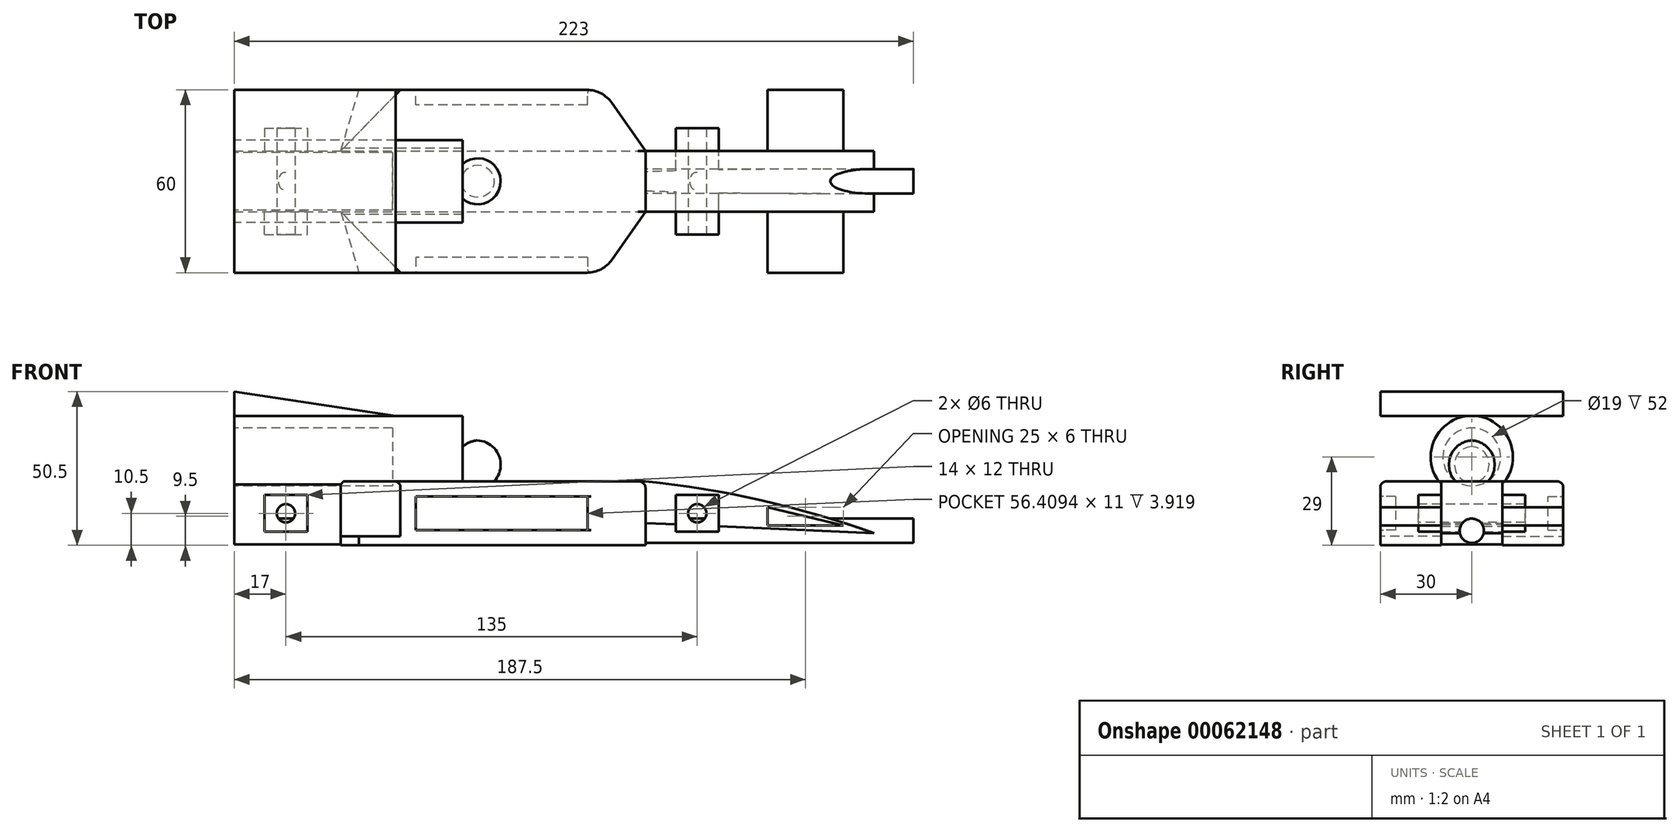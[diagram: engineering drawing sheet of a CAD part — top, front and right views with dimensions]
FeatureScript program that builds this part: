
annotation { "Feature Type Name" : "Feature", "Feature Type Description" : "" }
export const myFeature = defineFeature(function(context is Context, id is Id, definition is map)
    precondition{}
    {
        {
            var Q0;
            Q0=qCreatedBy(makeId("Front.planeOp"),FACE);
            var sketch = newSketch(context, id + "F0", { "sketchPlane" : qUnion([Q0])});
            skLineSegment(sketch, "E0.bottom", {"start": v(0, -8) * mm, "end": v(135, -8) * mm});
            skLineSegment(sketch, "E0.top", {"start": v(0, -28.73) * mm, "end": v(135, -28.73) * mm});
            skLineSegment(sketch, "E0.left", {"start": v(0, -8) * mm, "end": v(0, -28.73) * mm});
            skLineSegment(sketch, "E1", {"start": v(135, -28.73) * mm, "end": v(135, -21.73) * mm});
            skLineSegment(sketch, "E2", {"start": v(135, -21.73) * mm, "end": v(210, -25) * mm});
            skArc(sketch, "E3", {"start": v(210, -25) * mm, "mid": v(173.01, -14.23) * mm, "end": v(135, -8) * mm});
            skSolve(sketch);
        }
        {
            var Q0;
            Q0=makeQuery(id+"F0.imprint","IMPRINT",FACE,{"disambiguationData":[TD([[makeQuery(id+"F0.imprint","IMPRINT",EDGE,{"derivedFrom":sQuery(id+"F0.wireOp",EDGE,"E0.bottom")}),-1.0]])]});
            extrude(context, id + "F1", {"entities" : qUnion([Q0]), "depth" : 10 * mm});
        }
        {
            var Q0;
            Q0=makeQuery(id+"F1.opExtrude","SWEPT_FACE",FACE,{"disambiguationData":[OSD([sQuery(id+"F0.wireOp",EDGE,"E0.bottom")])]});
            var sketch = newSketch(context, id + "F2", { "sketchPlane" : qUnion([Q0])});
            skLineSegment(sketch, "E4", {"start": v(35, -10) * mm, "end": v(41, -30) * mm});
            skLineSegment(sketch, "E5", {"start": v(41, -30) * mm, "end": v(121, -30) * mm});
            skLineSegment(sketch, "E6", {"start": v(135, -10) * mm, "end": v(35, -10) * mm});
            skLineSegment(sketch, "E7", {"start": v(121, -30) * mm, "end": v(135, -10) * mm});
            skSolve(sketch);
        }
        {
            var Q0;
            Q0=makeQuery(id+"F2.imprint","IMPRINT",FACE,{"disambiguationData":[TD([[makeQuery(id+"F2.imprint","IMPRINT",EDGE,{"derivedFrom":sQuery(id+"F2.wireOp",EDGE,"E4")}),1.0]])]});
            extrude(context, id + "F3", {"entities" : qUnion([Q0]), "oppositeDirection" : true, "depth" : 21 * mm});
        }
        {
            var Q0;
            Q0=makeQuery(id+"F3.opExtrude","CAP_FACE",FACE,{"disambiguationData":[OSD([sQuery(id+"F2.wireOp",EDGE,"E4"),sQuery(id+"F2.wireOp",EDGE,"E5"),sQuery(id+"F2.wireOp",EDGE,"E6"),sQuery(id+"F2.wireOp",EDGE,"E7")])],"isStart":true});
            var sketch = newSketch(context, id + "F4", { "sketchPlane" : qUnion([Q0])});
            skLineSegment(sketch, "E8", {"start": v(0, -9.96) * mm, "end": v(35, -10) * mm});
            skLineSegment(sketch, "E9", {"start": v(35, -10) * mm, "end": v(72.36, -48.15) * mm});
            skLineSegment(sketch, "E10", {"start": v(72.36, -48.15) * mm, "end": v(0, -9.96) * mm});
            skSolve(sketch);
        }
        {
            var Q0;
            {var subQ1=makeQuery(id+"F3.opExtrude","CAP_EDGE",EDGE,{"disambiguationData":[OSD([sQuery(id+"F2.wireOp",EDGE,"E4")])],"isStart":true});Q0=makeQuery(id+"F4.imprint","IMPRINT",FACE,{"disambiguationData":[TD([[makeQuery(id+"F4.imprint","IMPRINT",EDGE,{"derivedFrom":subQ1}),1.0]])]});}
            extrude(context, id + "F5", {"entities" : qUnion([Q0]), "operationType" : NewBodyOperationType.REMOVE, "oppositeDirection" : true, "depth" : 18 * mm});
        }
        {
            var Q0;
            Q0=makeQuery(id+"F3.opExtrude","SWEPT_FACE",FACE,{"disambiguationData":[OSD([sQuery(id+"F2.wireOp",EDGE,"E5")])]});
            var sketch = newSketch(context, id + "F6", { "sketchPlane" : qUnion([Q0])});
            skLineSegment(sketch, "E11.0", {"start": v(59.59, -13) * mm, "end": v(59.59, -24) * mm});
            skLineSegment(sketch, "E11.2", {"start": v(59.59, -24) * mm, "end": v(116, -24) * mm});
            skLineSegment(sketch, "E11.4", {"start": v(116, -24) * mm, "end": v(116, -13) * mm});
            skLineSegment(sketch, "E11.5", {"start": v(116, -13) * mm, "end": v(59.59, -13) * mm});
            skSolve(sketch);
        }
        {
            var Q0;
            Q0=makeQuery(id+"F6.imprint","IMPRINT",FACE,{"disambiguationData":[TD([[makeQuery(id+"F6.imprint","IMPRINT",EDGE,{"derivedFrom":sQuery(id+"F6.wireOp",EDGE,"E11.0")}),1.0]])]});
            extrude(context, id + "F7", {"entities" : qUnion([Q0]), "operationType" : NewBodyOperationType.REMOVE, "oppositeDirection" : true, "depth" : 5 * mm});
        }
        {
            var Q0;
            Q0=qCreatedBy(makeId("Front.planeOp"),FACE);
            var sketch = newSketch(context, id + "F8", { "sketchPlane" : qUnion([Q0])});
            skLineSegment(sketch, "E12.bottom", {"start": v(0, 0) * mm, "end": v(75, 0) * mm});
            skLineSegment(sketch, "E12.top", {"start": v(0, 13.5) * mm, "end": v(75, 13.5) * mm});
            skLineSegment(sketch, "E12.left", {"start": v(0, 0) * mm, "end": v(0, 13.5) * mm});
            skLineSegment(sketch, "E12.right", {"start": v(75, 0) * mm, "end": v(75, 13.5) * mm});
            skSolve(sketch);
        }
        {
            var Q0;
            Q0=makeQuery(id+"F8.imprint","IMPRINT",FACE,{"disambiguationData":[TD([[makeQuery(id+"F8.imprint","IMPRINT",EDGE,{"derivedFrom":sQuery(id+"F8.wireOp",EDGE,"E12.bottom")}),1.0]])]});
            var Q1;
            Q1=sQuery(id+"F8.wireOp",EDGE,"E12.bottom");
            revolve(context, id + "F9", {"entities" : qUnion([Q0]), "axis" : qUnion([Q1]), "revolveType" : RevolveType.ONE_DIRECTION, "angle" : 180 * degree});
        }
        {
            var Q0;
            Q0=makeQuery(id+"F9.opRevolve","SWEPT_FACE",FACE,{"disambiguationData":[OSD([sQuery(id+"F8.wireOp",EDGE,"E12.left")])]});
            var sketch = newSketch(context, id + "F10", { "sketchPlane" : qUnion([Q0])});
            skArc(sketch, "E13", {"start": v(0, -9.5) * mm, "mid": v(9.5, 0) * mm, "end": v(0, 9.5) * mm});
            skLineSegment(sketch, "E14", {"start": v(0, 9.5) * mm, "end": v(0, -9.5) * mm});
            skSolve(sketch);
        }
        {
            var Q0;
            Q0=makeQuery(id+"F10.imprint","IMPRINT",FACE,{"disambiguationData":[TD([[makeQuery(id+"F10.imprint","IMPRINT",EDGE,{"derivedFrom":sQuery(id+"F10.wireOp",EDGE,"E13")}),1.0]])]});
            extrude(context, id + "F11", {"entities" : qUnion([Q0]), "operationType" : NewBodyOperationType.REMOVE, "oppositeDirection" : true, "depth" : 52 * mm});
        }
        {
            var Q0;
            Q0=qCreatedBy(makeId("Front.planeOp"),FACE);
            var sketch = newSketch(context, id + "F12", { "sketchPlane" : qUnion([Q0])});
            skLineSegment(sketch, "E15.bottom", {"start": v(145, -12.5) * mm, "end": v(159, -12.5) * mm});
            skLineSegment(sketch, "E15.top", {"start": v(145, -24.5) * mm, "end": v(159, -24.5) * mm});
            skLineSegment(sketch, "E15.left", {"start": v(145, -12.5) * mm, "end": v(145, -24.5) * mm});
            skLineSegment(sketch, "E15.right", {"start": v(159, -12.5) * mm, "end": v(159, -24.5) * mm});
            skLineSegment(sketch, "E16.1.0.0", {"start": v(24, -12.5) * mm, "end": v(24, -24.5) * mm});
            skLineSegment(sketch, "E16.1.0.1", {"start": v(10, -12.5) * mm, "end": v(24, -12.5) * mm});
            skLineSegment(sketch, "E16.1.0.2", {"start": v(10, -12.5) * mm, "end": v(10, -24.5) * mm});
            skLineSegment(sketch, "E16.1.0.3", {"start": v(10, -24.5) * mm, "end": v(24, -24.5) * mm});
            skLineSegment(sketch, "E16.direction1", {"start": v(159, -24.5) * mm, "end": v(24, -24.5) * mm, "construction": true});
            skSolve(sketch);
        }
        {
            var Q0;
            Q0 = qSketchRegion(id + "F12", true);
            extrude(context, id + "F13", {"entities" : qUnion([Q0]), "depth" : 17.5 * mm});
        }
        {
            var Q0;
            Q0=makeQuery(id+"F3.opExtrude","SWEPT_EDGE",EDGE,{"disambiguationData":[OSD([sQuery(id+"F2.wireOp",EDGE,"E5"),sQuery(id+"F2.wireOp",EDGE,"E7")])]});
            var Q1;
            Q1=makeQuery(id+"F5.boolean.opBoolean","COPY",EDGE,{"derivedFrom":makeQuery(id+"F5.opExtrude","SWEPT_EDGE",EDGE,{"disambiguationData":[OSD([sQuery(id+"F2.wireOp",EDGE,"E5"),sQuery(id+"F4.wireOp",EDGE,"E9")])]})});
            fillet(context, id + "F14", {"entities" : qUnion([Q0, Q1]), "radius" : 10 * mm, "tangentPropagation" : true, "allowEdgeOverflow" : false});
        }
        {
            var Q0;
            Q0=qCreatedBy(makeId("Front.planeOp"),FACE);
            var sketch = newSketch(context, id + "F15", { "sketchPlane" : qUnion([Q0])});
            skLineSegment(sketch, "E17", {"start": v(0, 13.5) * mm, "end": v(53, 13.5) * mm});
            skLineSegment(sketch, "E18", {"start": v(53, 13.5) * mm, "end": v(0, 21.5) * mm});
            skLineSegment(sketch, "E19", {"start": v(0, 21.5) * mm, "end": v(0, 13.5) * mm});
            skSolve(sketch);
        }
        {
            var Q0;
            Q0=makeQuery(id+"F15.imprint","IMPRINT",FACE,{"disambiguationData":[TD([[makeQuery(id+"F15.imprint","IMPRINT",EDGE,{"derivedFrom":sQuery(id+"F15.wireOp",EDGE,"E17")}),1.0]])]});
            extrude(context, id + "F16", {"entities" : qUnion([Q0]), "depth" : 30 * mm});
        }
        {
            var Q0;
            Q0=qCreatedBy(makeId("Front.planeOp"),FACE);
            var sketch = newSketch(context, id + "F17", { "sketchPlane" : qUnion([Q0])});
            skLineSegment(sketch, "E20", {"start": v(175, -22.5) * mm, "end": v(200, -22.5) * mm});
            skLineSegment(sketch, "E21", {"start": v(175, -22.5) * mm, "end": v(175, -16.5) * mm});
            skLineSegment(sketch, "E22", {"start": v(175, -16.5) * mm, "end": v(200, -22.5) * mm});
            skSolve(sketch);
        }
        {
            var Q0;
            Q0=makeQuery(id+"F17.imprint","IMPRINT",FACE,{"disambiguationData":[TD([[makeQuery(id+"F17.imprint","IMPRINT",EDGE,{"derivedFrom":sQuery(id+"F17.wireOp",EDGE,"E20")}),1.0]])]});
            extrude(context, id + "F18", {"entities" : qUnion([Q0]), "operationType" : NewBodyOperationType.ADD, "depth" : 30 * mm});
        }
        {
            var Q0;
            Q0=qCreatedBy(makeId("Front.planeOp"),FACE);
            var sketch = newSketch(context, id + "F19", { "sketchPlane" : qUnion([Q0])});
            skArc(sketch, "E23", {"start": v(80.22, -10.46) * mm, "mid": v(87.5, -2.27) * mm, "end": v(79.7, 5.41) * mm});
            skLineSegment(sketch, "E24", {"start": v(80.22, -10.46) * mm, "end": v(79.7, 5.41) * mm});
            skSolve(sketch);
        }
        {
            var Q0;
            Q0=makeQuery(id+"F19.imprint","IMPRINT",FACE,{"disambiguationData":[TD([[makeQuery(id+"F19.imprint","IMPRINT",EDGE,{"derivedFrom":sQuery(id+"F19.wireOp",EDGE,"E23")}),1.0]])]});
            var Q1;
            Q1=sQuery(id+"F19.wireOp",EDGE,"E24");
            revolve(context, id + "F20", {"operationType" : NewBodyOperationType.ADD, "entities" : qUnion([Q0]), "axis" : qUnion([Q1]), "revolveType" : RevolveType.ONE_DIRECTION, "oppositeDirection" : true, "angle" : 180 * degree});
        }
        {
            var Q0;
            Q0=makeQuery(id+"F13.opExtrude","CAP_FACE",FACE,{"disambiguationData":[OSD([sQuery(id+"F12.wireOp",EDGE,"E15.bottom"),sQuery(id+"F12.wireOp",EDGE,"E15.top"),sQuery(id+"F12.wireOp",EDGE,"E15.left"),sQuery(id+"F12.wireOp",EDGE,"E15.right")])],"isStart":false});
            var sketch = newSketch(context, id + "F21", { "sketchPlane" : qUnion([Q0])});
            skLineSegment(sketch, "E25", {"start": v(145, -12.5) * mm, "end": v(159, -24.5) * mm, "construction": true});
            skLineSegment(sketch, "E26", {"start": v(159, -12.5) * mm, "end": v(145, -24.5) * mm, "construction": true});
            skCircle(sketch, "E27", {"center": v(152, -18.5) * mm, "radius": 3 * mm});
            skCircle(sketch, "E28.1.0.0", {"center": v(17, -18.5) * mm, "radius": 3 * mm});
            skCircle(sketch, "E28.2.0.0", {"center": v(-118, -18.5) * mm, "radius": 3 * mm});
            skLineSegment(sketch, "E28.direction1", {"start": v(152, -18.5) * mm, "end": v(17, -18.5) * mm, "construction": true});
            skSolve(sketch);
        }
        {
            var Q0;
            Q0=makeQuery(id+"F21.imprint","IMPRINT",FACE,{"disambiguationData":[TD([[makeQuery(id+"F21.imprint","IMPRINT",EDGE,{"derivedFrom":sQuery(id+"F21.wireOp",EDGE,"E27")}),1.0]])]});
            var Q1;
            Q1=makeQuery(id+"F21.imprint","IMPRINT",FACE,{"disambiguationData":[TD([[makeQuery(id+"F21.imprint","IMPRINT",EDGE,{"derivedFrom":sQuery(id+"F21.wireOp",EDGE,"E28.1.0.0")}),1.0]])]});
            extrude(context, id + "F22", {"entities" : qUnion([Q0, Q1]), "operationType" : NewBodyOperationType.REMOVE, "oppositeDirection" : true, "depth" : 17.5 * mm});
        }
        {
            var Q0;
            Q0=makeQuery(id+"F3.opExtrude","CAP_EDGE",EDGE,{"disambiguationData":[OSD([sQuery(id+"F2.wireOp",EDGE,"E7")])],"isStart":true});
            fillet(context, id + "F23", {"entities" : qUnion([Q0]), "radius" : 2 * mm, "tangentPropagation" : true, "allowEdgeOverflow" : false});
        }
        {
            var Q0;
            Q0=makeQuery(id+"F7.boolean.opBoolean","COPY",EDGE,{"derivedFrom":makeQuery(id+"F7.opExtrude","CAP_EDGE",EDGE,{"disambiguationData":[OSD([sQuery(id+"F6.wireOp",EDGE,"E11.5")])],"isStart":true})});
            var Q1;
            Q1=makeQuery(id+"F14.opFillet","BLEND_EDGE",EDGE,{"blendedFrom":[makeQuery(id+"F3.opExtrude","SWEPT_EDGE",EDGE,{"disambiguationData":[OSD([sQuery(id+"F2.wireOp",EDGE,"E5"),sQuery(id+"F2.wireOp",EDGE,"E7")])]}),makeQuery(id+"F7.boolean.opBoolean","COPY",FACE,{"derivedFrom":makeQuery(id+"F7.opExtrude","SWEPT_FACE",FACE,{"disambiguationData":[OSD([sQuery(id+"F6.wireOp",EDGE,"E11.4")])]})})],"blendedInto":[makeQuery(id+"F7.boolean.opBoolean","COPY",FACE,{"derivedFrom":makeQuery(id+"F7.opExtrude","SWEPT_FACE",FACE,{"disambiguationData":[OSD([sQuery(id+"F6.wireOp",EDGE,"E11.4")])]})})]});
            var Q2;
            Q2=makeQuery(id+"F7.boolean.opBoolean","COPY",EDGE,{"derivedFrom":makeQuery(id+"F7.opExtrude","CAP_EDGE",EDGE,{"disambiguationData":[OSD([sQuery(id+"F6.wireOp",EDGE,"E11.2")])],"isStart":true})});
            fillet(context, id + "F24", {"entities" : qUnion([Q0, Q1, Q2]), "radius" : 1 * mm, "tangentPropagation" : true, "allowEdgeOverflow" : false});
        }
        {
            var Q0;
            Q0=makeQuery(id+"F1.opExtrude","SWEPT_BODY",BODY,{"disambiguationData":[OSD([sQuery(id+"F0.wireOp",EDGE,"E0.bottom"),sQuery(id+"F0.wireOp",EDGE,"E0.top"),sQuery(id+"F0.wireOp",EDGE,"E0.left"),sQuery(id+"F0.wireOp",EDGE,"E1"),sQuery(id+"F0.wireOp",EDGE,"E2"),sQuery(id+"F0.wireOp",EDGE,"E3")])]});
            var Q1;
            Q1=makeQuery(id+"F9.opRevolve","SWEPT_BODY",BODY,{"disambiguationData":[OSD([sQuery(id+"F8.wireOp",EDGE,"E12.bottom"),sQuery(id+"F8.wireOp",EDGE,"E12.top"),sQuery(id+"F8.wireOp",EDGE,"E12.left"),sQuery(id+"F8.wireOp",EDGE,"E12.right")])]});
            var Q2;
            Q2=makeQuery(id+"F16.opExtrude","SWEPT_BODY",BODY,{"disambiguationData":[OSD([sQuery(id+"F15.wireOp",EDGE,"E17"),sQuery(id+"F15.wireOp",EDGE,"E18"),sQuery(id+"F15.wireOp",EDGE,"E19")])]});
            var Q3;
            Q3=makeQuery(id+"F3.opExtrude","SWEPT_BODY",BODY,{"disambiguationData":[OSD([sQuery(id+"F2.wireOp",EDGE,"E4"),sQuery(id+"F2.wireOp",EDGE,"E5"),sQuery(id+"F2.wireOp",EDGE,"E6"),sQuery(id+"F2.wireOp",EDGE,"E7")])]});
            var Q4;
            Q4=makeQuery(id+"F13.opExtrude","SWEPT_BODY",BODY,{"disambiguationData":[OSD([sQuery(id+"F12.wireOp",EDGE,"E15.bottom"),sQuery(id+"F12.wireOp",EDGE,"E15.top"),sQuery(id+"F12.wireOp",EDGE,"E15.left"),sQuery(id+"F12.wireOp",EDGE,"E15.right")])]});
            var Q5;
            Q5=makeQuery(id+"F13.opExtrude","SWEPT_BODY",BODY,{"disambiguationData":[OSD([sQuery(id+"F12.wireOp",EDGE,"E16.1.0.0"),sQuery(id+"F12.wireOp",EDGE,"E16.1.0.1"),sQuery(id+"F12.wireOp",EDGE,"E16.1.0.2"),sQuery(id+"F12.wireOp",EDGE,"E16.1.0.3")])]});
            var Q6;
            Q6=qCreatedBy(makeId("Front.planeOp"),FACE);
            mirror(context, id + "F25", {"operationType" : NewBodyOperationType.ADD, "entities" : qUnion([Q0, Q1, Q2, Q3, Q4, Q5]), "mirrorPlane" : qUnion([Q6])});
        }
        {
            var Q0;
            Q0=qCreatedBy(makeId("Right.planeOp"),FACE);
            var sketch = newSketch(context, id + "F26", { "sketchPlane" : qUnion([Q0])});
            skCircle(sketch, "E29", {"center": v(0, -24.24) * mm, "radius": 4 * mm});
            skSolve(sketch);
        }
        {
            var Q0;
            Q0=makeQuery(id+"F26.imprint","IMPRINT",FACE,{"disambiguationData":[TD([[makeQuery(id+"F26.imprint","IMPRINT",EDGE,{"derivedFrom":sQuery(id+"F26.wireOp",EDGE,"E29")}),1.0]])]});
            extrude(context, id + "F27", {"entities" : qUnion([Q0]), "operationType" : NewBodyOperationType.ADD, "depth" : 223 * mm});
        }
    });
